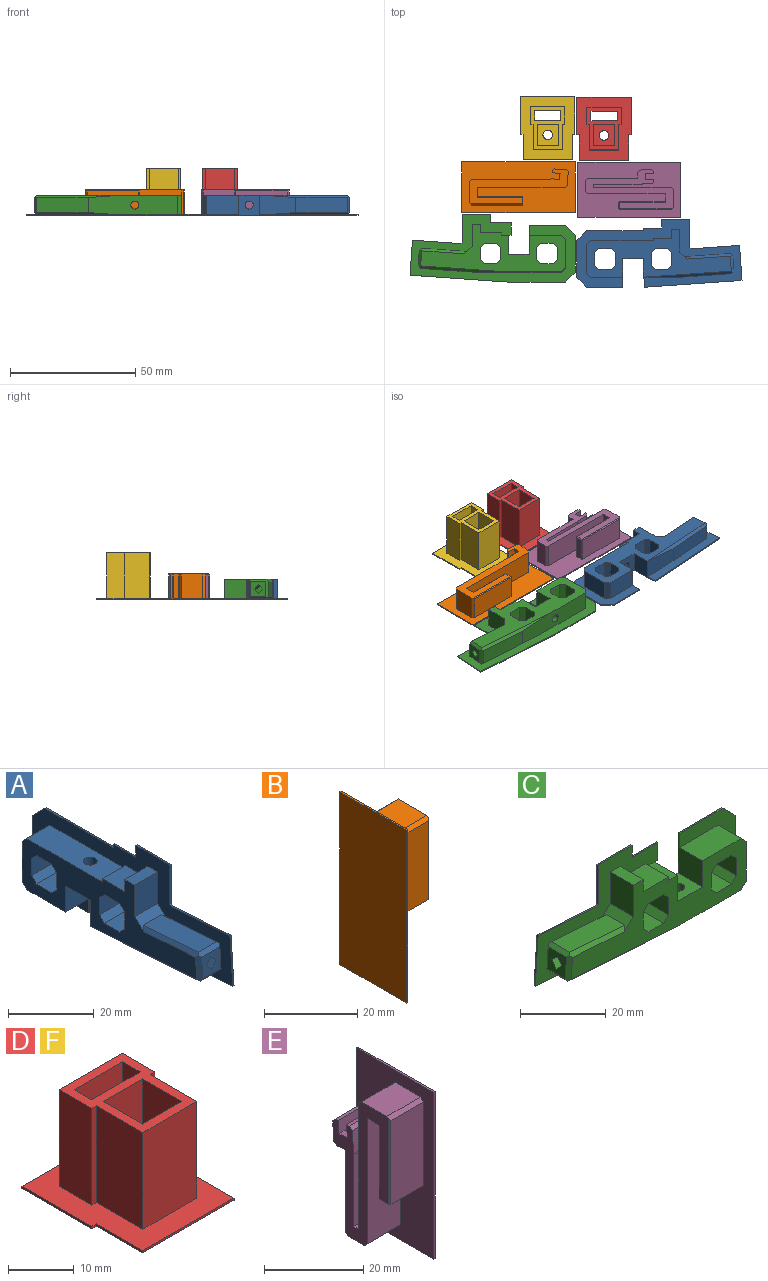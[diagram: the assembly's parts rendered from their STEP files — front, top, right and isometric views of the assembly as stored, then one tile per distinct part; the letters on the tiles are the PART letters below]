
ASSEMBLY  parts=6 mates=5
PART A: 66 faces, bbox 8x65.9x27 mm
  f0: plane 8.98x7.6mm, normal (0,-1,0), area 68.3mm2, adj f4,f5,f25,f64
  f1: plane 12.8x7.6mm, normal (0,0,-1), area 97.3mm2, adj f18,f25,f33,f64
  f2: plane 7.6x1mm, normal (0,1,0), area 7.6mm2, adj f20,f21,f25,f64
  f3: plane 7.6x3.4mm, normal (0,1,0), area 25.8mm2, adj f4,f21,f25,f64
  f4: plane 7.6x3.2mm, normal (0,0,1), area 24.3mm2, adj f0,f3,f25,f64
  f5: plane 7.6x3mm, normal (0,-0.68,0.73), area 21.7mm2, adj f0,f13,f25,f43,f45,f64
  f6: plane 6x5.99mm, normal (0,-1,0.07), area 30.2mm2, adj f26,f27,f28,f29,f46,f47,f48,f49
  f7: plane 8x5mm, normal (0,0,1), area 40mm2, adj f24,f25,f37,f38
  f8: plane 8x5mm, normal (0,1,0), area 40mm2, adj f24,f25,f37,f39
  f9: plane 8x5mm, normal (0,0,-1), area 40mm2, adj f24,f25,f39,f41
  f10: plane 8x5mm, normal (0,0,1), area 40mm2, adj f24,f25,f34,f36
  f11: plane 8x5mm, normal (0,1,0), area 40mm2, adj f24,f25,f35,f36
  f12: plane 8x5mm, normal (0,0,-1), area 40mm2, adj f24,f25,f35,f40
  f13: plane 18.01x6mm, normal (0,0.07,1), area 108.3mm2, adj f5,f43,f45,f46
  f14: plane 20.56x6mm, normal (0,-0.07,-1), area 123.7mm2, adj f15,f42,f44,f49
  f15: plane 14.5x8mm, normal (0,0,-1), area 100.5mm2, adj f14,f16,f24,f25,f42,f44,f50,f64
  f16: plane 8x7.45mm, normal (0,1,0), area 59.6mm2, adj f15,f17,f24,f25
  f17: plane 8.2x8mm, normal (0,0,-1), area 57.6mm2, adj f16,f18,f24,f25,f31
  f18: plane 11.45x8mm, normal (0,-1,0), area 61.2mm2, adj f1,f17,f24,f25,f64,f65
  f19: plane 11.4x7.6mm, normal (0,1,0), area 86.6mm2, adj f25,f32,f33,f64
  f20: plane 24.9x7.6mm, normal (0,0,1), area 181.2mm2, adj f2,f25,f31,f32,f64
  f21: plane 7.6x7.4mm, normal (0,0,1), area 56.2mm2, adj f2,f3,f25,f64
  f22: plane 8x5mm, normal (0,-1,0), area 40mm2, adj f24,f25,f34,f40
  f23: plane 8x5mm, normal (0,-1,0), area 40mm2, adj f24,f25,f38,f41
  f24: plane 65.86x27mm, normal (1,0,0), area 1114.1mm2, adj f7,f8,f9,f10,f11,f12,f15,f16
  f25: plane 57.59x19mm, normal (-1,0,0), area 494.5mm2, adj f0,f1,f2,f3,f4,f5,f7,f8
  f26: plane 20.07x3.09mm, normal (0.71,0.05,0.71), area 48.1mm2, adj f6,f27,f29,f30
  f27: plane 20.07x3.09mm, normal (-0.71,0.05,0.71), area 48.1mm2, adj f6,f26,f28,f30
  f28: plane 20.07x3.09mm, normal (-0.71,-0.05,-0.71), area 48.1mm2, adj f6,f27,f29,f30
  f29: plane 20.07x3.09mm, normal (0.71,-0.05,-0.71), area 48.1mm2, adj f6,f26,f28,f30
  f30: plane 3.4x3.39mm, normal (0,-1,0.07), area 5.8mm2, adj f26,f27,f28,f29
  f31: cylinder r=1.6mm len=7.15mm, axis (0,0,1), area 71.9mm2, adj f17,f20
  f32: plane 7.6x1.6mm, normal (0,0.71,0.71), area 17.2mm2, adj f19,f20,f25,f64
  f33: plane 7.6x1.6mm, normal (0,0.71,-0.71), area 17.2mm2, adj f1,f19,f25,f64
  f34: plane 8x1.6mm, normal (0,-0.71,0.71), area 18.1mm2, adj f10,f22,f24,f25
  f35: plane 8x1.6mm, normal (0,0.71,-0.71), area 18.1mm2, adj f11,f12,f24,f25
  f36: plane 8x1.6mm, normal (0,0.71,0.71), area 18.1mm2, adj f10,f11,f24,f25
  f37: plane 8x1.6mm, normal (0,0.71,0.71), area 18.1mm2, adj f7,f8,f24,f25
  f38: plane 8x1.6mm, normal (0,-0.71,0.71), area 18.1mm2, adj f7,f23,f24,f25
  f39: plane 8x1.6mm, normal (0,0.71,-0.71), area 18.1mm2, adj f8,f9,f24,f25
  f40: plane 8x1.6mm, normal (0,-0.71,-0.71), area 18.1mm2, adj f12,f22,f24,f25
  f41: plane 8x1.6mm, normal (0,-0.71,-0.71), area 18.1mm2, adj f9,f23,f24,f25
  f42: plane 29.63x2.06mm, normal (0.71,-0.05,-0.71), area 21.4mm2, adj f14,f15,f47,f49,f64
  f43: plane 18.54x2.19mm, normal (-0.71,0.05,0.71), area 25.2mm2, adj f5,f13,f25,f46,f48
  f44: plane 35.36x2.44mm, normal (-0.71,-0.05,-0.71), area 39.6mm2, adj f14,f15,f25,f48,f49
  f45: plane 18.54x1.82mm, normal (0.71,0.05,0.71), area 15.3mm2, adj f5,f13,f46,f47,f64
  f46: plane 7x1.07mm, normal (0,-0.66,0.75), area 9.2mm2, adj f6,f13,f43,f45,f47,f48
  f47: plane 6.98x1.05mm, normal (0.71,-0.71,0.05), area 5.6mm2, adj f6,f42,f45,f46,f49,f64
  f48: plane 6.98x1.42mm, normal (-0.71,-0.71,0.05), area 9.2mm2, adj f6,f25,f43,f44,f46,f49
  f49: plane 7x1.07mm, normal (0,-0.75,-0.66), area 9.2mm2, adj f6,f14,f42,f44,f47,f48
  f50: plane 3.99x0.4mm, normal (0,1,-0.07), area 1.6mm2, adj f15,f24,f51,f64
  f51: plane 38.82x2.71mm, normal (0,-0.07,-1), area 15.6mm2, adj f24,f50,f52,f64
  f52: plane 13.97x0.98mm, normal (0,-1,0.07), area 5.6mm2, adj f24,f51,f53,f64
  f53: plane 19.33x1.35mm, normal (0,0.07,1), area 7.8mm2, adj f24,f52,f54,f64
  f54: plane 0.45x0.42mm, normal (0,-0.68,0.73), area 0.2mm2, adj f24,f53,f55,f64
  f55: plane 11.24x0.4mm, normal (0,-1,0), area 4.5mm2, adj f24,f54,f56,f64
  f56: plane 11.2x0.4mm, normal (0,0,1), area 4.5mm2, adj f24,f55,f57,f64
  f57: plane 3.4x0.4mm, normal (0,1,0), area 1.4mm2, adj f24,f56,f58,f64
  f58: plane 7.4x0.4mm, normal (0,0,1), area 3mm2, adj f24,f57,f59,f64
  f59: plane 1x0.4mm, normal (0,1,0), area 0.4mm2, adj f24,f58,f60,f64
  f60: plane 22.56x0.4mm, normal (0,0,1), area 9mm2, adj f24,f59,f61,f64
  f61: plane 3.94x3.94mm, normal (0,0.71,0.71), area 2.2mm2, adj f24,f60,f62,f64
  f62: plane 14.71x0.4mm, normal (0,1,0), area 5.9mm2, adj f24,f61,f63,f64
  f63: plane 3.94x3.94mm, normal (0,0.71,-0.71), area 2.2mm2, adj f24,f62,f64,f65
  f64: plane 65.86x27mm, normal (-1,0,0), area 597.1mm2, adj f0,f1,f2,f3,f4,f5,f15,f18
  f65: plane 14.46x0.4mm, normal (0,0,-1), area 5.8mm2, adj f18,f24,f63,f64
PART B: 33 faces, bbox 10x20.2x45.3 mm
  f0: plane 9.6x4mm, normal (0,0,-1), area 34.6mm2, adj f1,f16,f19,f20,f27
  f1: plane 35.04x9.6mm, normal (0,-1,0), area 336.4mm2, adj f0,f11,f19,f27
  f2: plane 9.6x5.42mm, normal (0,-0.07,-1), area 52.2mm2, adj f11,f15,f19,f27
  f3: plane 9.6x4.79mm, normal (0,1,-0.07), area 46.1mm2, adj f14,f15,f19,f27
  f4: plane 9.6x0.8mm, normal (0,0.07,1), area 7.7mm2, adj f5,f14,f19,f27
  f5: plane 9.6x3.19mm, normal (0,-1,0.07), area 30.7mm2, adj f4,f6,f19,f27
  f6: plane 9.6x2.39mm, normal (0,0.07,1), area 23mm2, adj f5,f7,f19,f27
  f7: plane 9.6x3.19mm, normal (0,1,-0.07), area 30.7mm2, adj f6,f8,f19,f27
  f8: plane 9.6x0.5mm, normal (0,0.91,0.41), area 5.2mm2, adj f7,f9,f19,f27
  f9: plane 31.51x9.6mm, normal (0,1,0), area 302.5mm2, adj f8,f13,f19,f27
  f10: plane 9.6x8.6mm, normal (0,0,1), area 82.6mm2, adj f12,f13,f19,f27
  f11: plane 9.6x0.8mm, normal (0,-0.73,-0.68), area 10.5mm2, adj f1,f2,f19,f27
  f12: plane 9.6x0.8mm, normal (0,-0.71,0.71), area 10.7mm2, adj f10,f17,f19,f26,f27
  f13: plane 9.6x0.8mm, normal (0,0.71,0.71), area 10.9mm2, adj f9,f10,f19,f27
  f14: plane 9.6x0.85mm, normal (0,0.75,0.66), area 10.9mm2, adj f3,f4,f19,f27
  f15: plane 9.6x0.85mm, normal (0,0.66,-0.75), area 10.9mm2, adj f2,f3,f19,f27
  f16: plane 18.2x9.2mm, normal (0,1,0), area 167.4mm2, adj f0,f20,f21,f27
  f17: plane 20.6x9.2mm, normal (0,-1,0), area 189.5mm2, adj f12,f24,f26,f27
  f18: plane 9.2x2.6mm, normal (0,0,-1), area 23.9mm2, adj f21,f23,f24,f27
  f19: plane 39.42x13.96mm, normal (1,0,0), area 210.2mm2, adj f0,f1,f2,f3,f4,f5,f6,f7
  f20: plane 18.2x0.4mm, normal (0.71,0.71,0), area 10.3mm2, adj f0,f16,f19,f22
  f21: plane 9.2x0.4mm, normal (0,0.71,-0.71), area 5.2mm2, adj f16,f18,f22,f27
  f22: plane 0.4x0.4mm, normal (0.58,0.58,-0.58), area 0.1mm2, adj f20,f21,f23
  f23: plane 2.6x0.4mm, normal (0.71,0,-0.71), area 1.5mm2, adj f18,f19,f22,f25
  f24: plane 9.2x0.4mm, normal (0,-0.71,-0.71), area 5.2mm2, adj f17,f18,f25,f27
  f25: plane 0.4x0.4mm, normal (0.58,-0.58,-0.58), area 0.1mm2, adj f23,f24,f26
  f26: plane 21x0.4mm, normal (0.71,-0.71,0), area 11.8mm2, adj f12,f17,f19,f25
  f27: plane 45.28x20.19mm, normal (1,0,0), area 687.1mm2, adj f0,f1,f2,f3,f4,f5,f6,f7
  f28: plane 45.28x0.4mm, normal (0,-1,0), area 18.1mm2, adj f27,f29,f31,f32
  f29: plane 20.19x0.4mm, normal (0,0,1), area 8.1mm2, adj f27,f28,f30,f32
  f30: plane 45.28x0.4mm, normal (0,1,0), area 18.1mm2, adj f27,f29,f31,f32
  f31: plane 20.19x0.4mm, normal (0,0,-1), area 8.1mm2, adj f27,f28,f30,f32
  f32: plane 45.28x20.19mm, normal (-1,0,0), area 914.1mm2, adj f28,f29,f30,f31
PART C: 66 faces, bbox 65.9x8x27 mm
  f0: plane 6x5.99mm, normal (-1,0,0.07), area 30.2mm2, adj f25,f26,f27,f28,f46,f47,f48,f49
  f1: plane 8x5mm, normal (0,0,1), area 40mm2, adj f23,f24,f39,f40
  f2: plane 8x5mm, normal (1,0,0), area 40mm2, adj f23,f24,f38,f40
  f3: plane 8x5mm, normal (0,0,-1), area 40mm2, adj f23,f24,f38,f41
  f4: plane 8x5mm, normal (0,0,1), area 40mm2, adj f23,f24,f34,f35
  f5: plane 8x5mm, normal (1,0,0), area 40mm2, adj f23,f24,f35,f36
  f6: plane 8x5mm, normal (0,0,-1), area 40mm2, adj f23,f24,f36,f37
  f7: plane 8.98x7.6mm, normal (-1,0,0), area 68.3mm2, adj f21,f23,f31,f51
  f8: plane 18.01x6mm, normal (0.07,0,1), area 108.3mm2, adj f31,f42,f45,f46
  f9: plane 20.56x6mm, normal (-0.07,0,-1), area 123.7mm2, adj f10,f43,f44,f49
  f10: plane 35.5x7.6mm, normal (0,0,-1), area 252mm2, adj f9,f23,f30,f32,f43,f44,f51
  f11: plane 11.4x7.6mm, normal (1,0,0), area 86.6mm2, adj f23,f32,f33,f51
  f12: plane 12.8x7.6mm, normal (0,0,1), area 97.3mm2, adj f13,f23,f33,f51
  f13: plane 11.45x8mm, normal (-1,0,0), area 61.2mm2, adj f12,f14,f23,f24,f51,f52
  f14: plane 8.2x8mm, normal (0,0,1), area 57.6mm2, adj f13,f15,f23,f24,f30
  f15: plane 8x7.45mm, normal (1,0,0), area 59.6mm2, adj f14,f16,f23,f24,f50
  f16: plane 7.6x2.9mm, normal (0,0,1), area 22mm2, adj f15,f17,f23,f51
  f17: plane 7.6x1mm, normal (1,0,0), area 7.6mm2, adj f16,f18,f23,f51
  f18: plane 8.4x7.6mm, normal (0,0,1), area 63.8mm2, adj f17,f19,f23,f51
  f19: plane 7.6x3.4mm, normal (1,0,0), area 25.8mm2, adj f18,f21,f23,f51
  f20: plane 8x5mm, normal (-1,0,0), area 40mm2, adj f23,f24,f34,f37
  f21: plane 7.6x3.2mm, normal (0,0,1), area 24.3mm2, adj f7,f19,f23,f51
  f22: plane 8x5mm, normal (-1,0,0), area 40mm2, adj f23,f24,f39,f41
  f23: plane 57.59x19mm, normal (0,-1,0), area 495.5mm2, adj f1,f2,f3,f4,f5,f6,f7,f10
  f24: plane 65.86x27mm, normal (0,1,0), area 1120.7mm2, adj f1,f2,f3,f4,f5,f6,f13,f14
  f25: plane 20.07x3.09mm, normal (0.05,-0.71,0.71), area 48.1mm2, adj f0,f26,f28,f29
  f26: plane 20.07x3.09mm, normal (0.05,0.71,0.71), area 48.1mm2, adj f0,f25,f27,f29
  f27: plane 20.07x3.09mm, normal (-0.05,0.71,-0.71), area 48.1mm2, adj f0,f26,f28,f29
  f28: plane 20.07x3.09mm, normal (-0.05,-0.71,-0.71), area 48.1mm2, adj f0,f25,f27,f29
  f29: plane 3.4x3.39mm, normal (-1,0,0.07), area 5.8mm2, adj f25,f26,f27,f28
  f30: cylinder r=1.6mm len=7.15mm, axis (0,0,1), area 71.9mm2, adj f10,f14
  f31: plane 7.6x3mm, normal (-0.68,0,0.73), area 21.7mm2, adj f7,f8,f23,f42,f45,f51
  f32: plane 7.6x1.6mm, normal (0.71,0,-0.71), area 17.2mm2, adj f10,f11,f23,f51
  f33: plane 7.6x1.6mm, normal (0.71,0,0.71), area 17.2mm2, adj f11,f12,f23,f51
  f34: plane 8x1.6mm, normal (-0.71,0,0.71), area 18.1mm2, adj f4,f20,f23,f24
  f35: plane 8x1.6mm, normal (0.71,0,0.71), area 18.1mm2, adj f4,f5,f23,f24
  f36: plane 8x1.6mm, normal (0.71,0,-0.71), area 18.1mm2, adj f5,f6,f23,f24
  f37: plane 8x1.6mm, normal (-0.71,0,-0.71), area 18.1mm2, adj f6,f20,f23,f24
  f38: plane 8x1.6mm, normal (0.71,0,-0.71), area 18.1mm2, adj f2,f3,f23,f24
  f39: plane 8x1.6mm, normal (-0.71,0,0.71), area 18.1mm2, adj f1,f22,f23,f24
  f40: plane 8x1.6mm, normal (0.71,0,0.71), area 18.1mm2, adj f1,f2,f23,f24
  f41: plane 8x1.6mm, normal (-0.71,0,-0.71), area 18.1mm2, adj f3,f22,f23,f24
  f42: plane 18.54x1.82mm, normal (0.05,0.71,0.71), area 15.3mm2, adj f8,f31,f46,f48,f51
  f43: plane 29.63x2.06mm, normal (-0.05,0.71,-0.71), area 21.4mm2, adj f9,f10,f48,f49,f51
  f44: plane 35.36x2.44mm, normal (-0.05,-0.71,-0.71), area 39.6mm2, adj f9,f10,f23,f47,f49
  f45: plane 18.54x2.19mm, normal (0.05,-0.71,0.71), area 25.2mm2, adj f8,f23,f31,f46,f47
  f46: plane 7x1.07mm, normal (-0.66,0,0.75), area 9.2mm2, adj f0,f8,f42,f45,f47,f48
  f47: plane 6.98x1.42mm, normal (-0.71,-0.71,0.05), area 9.2mm2, adj f0,f23,f44,f45,f46,f49
  f48: plane 6.98x1.05mm, normal (-0.71,0.71,0.05), area 5.6mm2, adj f0,f42,f43,f46,f49,f51
  f49: plane 7x1.07mm, normal (-0.75,0,-0.66), area 9.2mm2, adj f0,f9,f43,f44,f47,f48
  f50: plane 1.1x0.4mm, normal (0,0,-1), area 0.4mm2, adj f15,f24,f51,f65
  f51: plane 65.86x27mm, normal (0,-1,0), area 602.9mm2, adj f7,f10,f11,f12,f13,f16,f17,f18
  f52: plane 14.46x0.4mm, normal (0,0,1), area 5.8mm2, adj f13,f24,f51,f53
  f53: plane 3.94x3.94mm, normal (0.71,0,0.71), area 2.2mm2, adj f24,f51,f52,f54
  f54: plane 14.71x0.4mm, normal (1,0,0), area 5.9mm2, adj f24,f51,f53,f55
  f55: plane 3.94x3.94mm, normal (0.71,0,-0.71), area 2.2mm2, adj f24,f51,f54,f56
  f56: plane 22.96x0.4mm, normal (0,0,-1), area 9.2mm2, adj f24,f51,f55,f57
  f57: plane 38.96x2.72mm, normal (-0.07,0,-1), area 15.6mm2, adj f24,f51,f56,f58
  f58: plane 13.97x0.98mm, normal (-1,0,0.07), area 5.6mm2, adj f24,f51,f57,f59
  f59: plane 19.33x1.35mm, normal (0.07,0,1), area 7.8mm2, adj f24,f51,f58,f60
  f60: plane 0.45x0.42mm, normal (-0.68,0,0.73), area 0.2mm2, adj f24,f51,f59,f61
  f61: plane 11.24x0.4mm, normal (-1,0,0), area 4.5mm2, adj f24,f51,f60,f62
  f62: plane 11.2x0.4mm, normal (0,0,1), area 4.5mm2, adj f24,f51,f61,f63
  f63: plane 3.4x0.4mm, normal (1,0,0), area 1.4mm2, adj f24,f51,f62,f64
  f64: plane 8.4x0.4mm, normal (0,0,1), area 3.4mm2, adj f24,f51,f63,f65
  f65: plane 5x0.4mm, normal (1,0,0), area 2mm2, adj f24,f50,f51,f64
PART D: 30 faces, bbox 21.6x25x18.4 mm
  f0: plane 18.4x3.8mm, normal (-1,0,0), area 69.9mm2, adj f1,f15,f16,f18
  f1: plane 18.4x10.4mm, normal (0,1,0), area 191.4mm2, adj f0,f2,f16,f18
  f2: plane 18.4x3.8mm, normal (1,0,0), area 69.9mm2, adj f1,f15,f16,f18
  f3: plane 18x1mm, normal (0,-1,0), area 18mm2, adj f4,f13,f16,f29
  f4: plane 18x10mm, normal (-1,0,0), area 180mm2, adj f3,f5,f16,f29
  f5: plane 18x11.6mm, normal (0,-1,0), area 208.8mm2, adj f4,f6,f16,f29
  f6: plane 18x10mm, normal (1,0,0), area 180mm2, adj f5,f7,f16,f29
  f7: plane 18x1mm, normal (0,-1,0), area 18mm2, adj f6,f8,f16,f29
  f8: plane 18x7mm, normal (1,0,0), area 126mm2, adj f7,f9,f16,f29
  f9: plane 18x13.6mm, normal (0,1,0), area 244.8mm2, adj f8,f13,f16,f29
  f10: plane 16x8.4mm, normal (1,0,0), area 134.4mm2, adj f11,f14,f16,f19
  f11: plane 16x8.4mm, normal (0,-1,0), area 134.4mm2, adj f10,f12,f16,f19
  f12: plane 16x8.4mm, normal (-1,0,0), area 134.4mm2, adj f11,f14,f16,f19
  f13: plane 18x7mm, normal (-1,0,0), area 126mm2, adj f3,f9,f16,f29
  f14: plane 16x8.4mm, normal (0,1,0), area 134.4mm2, adj f10,f12,f16,f19
  f15: plane 18.4x10.4mm, normal (0,-1,0), area 191.4mm2, adj f0,f2,f16,f18
  f16: plane 17x13.6mm, normal (0,0,1), area 101.1mm2, adj f0,f1,f2,f3,f4,f5,f6,f7
  f17: cylinder r=1.9mm len=3.8mm, axis (0,0,1), area 23.9mm2, adj f19,f20
  f18: plane 25x21.6mm, normal (0,0,-1), area 463.9mm2, adj f0,f1,f2,f15,f20,f21,f22,f23
  f19: plane 8.4x8.4mm, normal (0,0,1), area 59.2mm2, adj f10,f11,f12,f14,f17
  f20: cone r=2.3mm half-angle=45deg, axis (0,0,-1), area 7.5mm2, adj f17,f18
  f21: plane 21.6x0.4mm, normal (0,1,0), area 8.6mm2, adj f18,f22,f23,f29
  f22: plane 15x0.4mm, normal (-1,0,0), area 6mm2, adj f18,f21,f24,f29
  f23: plane 15x0.4mm, normal (1,0,0), area 6mm2, adj f18,f21,f25,f29
  f24: plane 1x0.4mm, normal (0,-1,0), area 0.4mm2, adj f18,f22,f26,f29
  f25: plane 1x0.4mm, normal (0,-1,0), area 0.4mm2, adj f18,f23,f27,f29
  f26: plane 10x0.4mm, normal (-1,0,0), area 4mm2, adj f18,f24,f28,f29
  f27: plane 10x0.4mm, normal (1,0,0), area 4mm2, adj f18,f25,f28,f29
  f28: plane 19.6x0.4mm, normal (0,-1,0), area 7.8mm2, adj f18,f26,f27,f29
  f29: plane 25x21.6mm, normal (0,0,1), area 308.8mm2, adj f3,f4,f5,f6,f7,f8,f9,f13
PART E: 40 faces, bbox 10x22x41 mm
  f0: plane 9.6x3.4mm, normal (0,0,-1), area 28.9mm2, adj f1,f23,f26,f33,f34
  f1: plane 31x9.6mm, normal (0,-1,0), area 297.6mm2, adj f0,f16,f26,f34
  f2: plane 9.6x4.6mm, normal (0,0,-1), area 44.2mm2, adj f16,f17,f26,f34
  f3: plane 20.03x9.6mm, normal (0,1,0), area 192.3mm2, adj f4,f17,f26,f34
  f4: plane 9.6x2.39mm, normal (0,-0.07,-1), area 23mm2, adj f3,f21,f26,f34
  f5: plane 9.6x4.79mm, normal (0,1,-0.07), area 46.1mm2, adj f21,f22,f26,f34
  f6: plane 9.6x0.8mm, normal (0,0.07,1), area 7.7mm2, adj f7,f22,f26,f34
  f7: plane 9.6x3.19mm, normal (0,-1,0.07), area 30.7mm2, adj f6,f8,f26,f34
  f8: plane 9.6x2.39mm, normal (0,0.07,1), area 23mm2, adj f7,f9,f26,f34
  f9: plane 9.6x3.19mm, normal (0,1,-0.07), area 30.7mm2, adj f8,f10,f26,f34
  f10: plane 9.6x0.8mm, normal (0,0.07,1), area 7.7mm2, adj f9,f20,f26,f34
  f11: plane 9.6x5.59mm, normal (0,-1,0.07), area 53.8mm2, adj f12,f20,f26,f34
  f12: plane 17.8x9.6mm, normal (0,-1,0), area 170.9mm2, adj f11,f13,f26,f34
  f13: plane 9.6x1.4mm, normal (0,0,1), area 13.4mm2, adj f12,f14,f26,f34
  f14: plane 31x9.6mm, normal (0,1,0), area 297.6mm2, adj f13,f18,f26,f34
  f15: plane 9.6x7.2mm, normal (0,0,1), area 69.1mm2, adj f18,f19,f26,f34
  f16: plane 9.6x0.8mm, normal (0,-0.71,-0.71), area 10.9mm2, adj f1,f2,f26,f34
  f17: plane 9.6x0.8mm, normal (0,0.71,-0.71), area 10.9mm2, adj f2,f3,f26,f34
  f18: plane 9.6x0.8mm, normal (0,0.71,0.71), area 10.9mm2, adj f14,f15,f26,f34
  f19: plane 9.6x0.8mm, normal (0,-0.71,0.71), area 10.7mm2, adj f15,f24,f26,f27,f34
  f20: plane 9.6x0.85mm, normal (0,-0.66,0.75), area 10.9mm2, adj f10,f11,f26,f34
  f21: plane 9.6x0.85mm, normal (0,0.66,-0.75), area 10.9mm2, adj f4,f5,f26,f34
  f22: plane 9.6x0.85mm, normal (0,0.75,0.66), area 10.9mm2, adj f5,f6,f26,f34
  f23: plane 18.2x9.2mm, normal (0,1,0), area 167.4mm2, adj f0,f31,f33,f34
  f24: plane 20.6x9.2mm, normal (0,-1,0), area 189.5mm2, adj f19,f27,f28,f34
  f25: plane 9.2x2.6mm, normal (0,0,-1), area 23.9mm2, adj f28,f30,f31,f34
  f26: plane 35x15.78mm, normal (-1,0,0), area 231.4mm2, adj f0,f1,f2,f3,f4,f5,f6,f7
  f27: plane 21x0.4mm, normal (-0.71,-0.71,0), area 11.8mm2, adj f19,f24,f26,f29
  f28: plane 9.2x0.4mm, normal (0,-0.71,-0.71), area 5.2mm2, adj f24,f25,f29,f34
  f29: plane 0.4x0.4mm, normal (-0.58,-0.58,-0.58), area 0.1mm2, adj f27,f28,f30
  f30: plane 2.6x0.4mm, normal (-0.71,0,-0.71), area 1.5mm2, adj f25,f26,f29,f32
  f31: plane 9.2x0.4mm, normal (0,0.71,-0.71), area 5.2mm2, adj f23,f25,f32,f34
  f32: plane 0.4x0.4mm, normal (-0.58,0.58,-0.58), area 0.1mm2, adj f30,f31,f33
  f33: plane 18.2x0.4mm, normal (-0.71,0.71,0), area 10.3mm2, adj f0,f23,f26,f32
  f34: plane 41x22.01mm, normal (-1,0,0), area 654.2mm2, adj f0,f1,f2,f3,f4,f5,f6,f7
  f35: plane 22.01x0.4mm, normal (0,0,1), area 8.8mm2, adj f34,f36,f38,f39
  f36: plane 41x0.4mm, normal (0,-1,0), area 16.4mm2, adj f34,f35,f37,f39
  f37: plane 22.01x0.4mm, normal (0,0,-1), area 8.8mm2, adj f34,f36,f38,f39
  f38: plane 41x0.4mm, normal (0,1,0), area 16.4mm2, adj f34,f35,f37,f39
  f39: plane 41x22.01mm, normal (1,0,0), area 902.4mm2, adj f35,f36,f37,f38
PART F: same geometry as D
PLACE A rot(axis=(-0.58,0.58,0.58),120deg) t=(22.22,0.93,-4.07)mm
PLACE B rot(axis=(0,-1,0),90deg) t=(-23.69,-0.49,21.93)mm
PLACE C rot(axis=(-1,0,0),90deg) t=(-23.36,3,-4.07)mm
PLACE D t=(10.61,33.22,-5.67)mm
PLACE E rot(axis=(0,1,0),90deg) t=(18.77,-2.45,21.93)mm
PLACE F t=(-11.82,33.46,-5.67)mm
MATE planar D.f18 <-> B.f32  axis (0,0,-1) through (10.61,23.42,-8.07)mm
MATE planar D.f18 <-> A.f24  axis (0,0,-1) through (20.91,33.42,-8.07)mm
MATE planar D.f18 <-> E.f39  axis (0,0,-1) through (20.41,33.42,-8.07)mm
MATE planar D.f18 <-> F.f18  axis (0,0,-1) through (20.41,33.42,-8.07)mm
MATE planar D.f18 <-> C.f24  axis (0,0,-1) through (5.41,39.02,-8.07)mm
